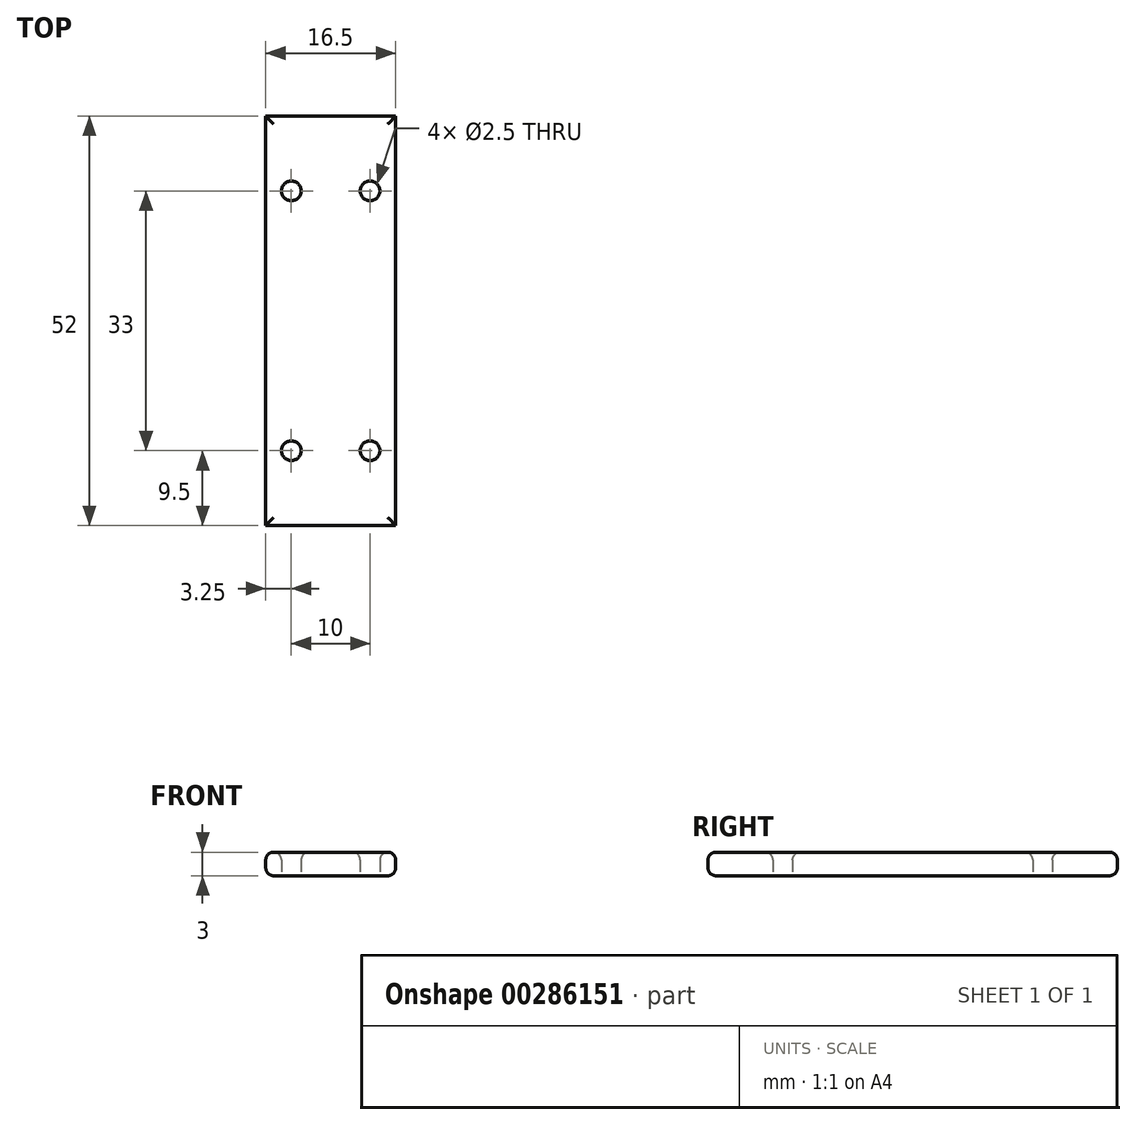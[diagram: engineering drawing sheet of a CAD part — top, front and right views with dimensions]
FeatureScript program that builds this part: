
annotation { "Feature Type Name" : "Feature", "Feature Type Description" : "" }
export const myFeature = defineFeature(function(context is Context, id is Id, definition is map)
    precondition{}
    {
        {
            var Q0;
            Q0=qCreatedBy(makeId("Top.planeOp"),FACE);
            var sketch = newSketch(context, id + "F0", { "sketchPlane" : qUnion([Q0])});
            skLineSegment(sketch, "E0.bottom", {"start": v(0, 0) * mm, "end": v(16.5, 0) * mm});
            skLineSegment(sketch, "E0.top", {"start": v(0, 52) * mm, "end": v(16.5, 52) * mm});
            skLineSegment(sketch, "E0.left", {"start": v(0, 0) * mm, "end": v(0, 52) * mm});
            skLineSegment(sketch, "E0.right", {"start": v(16.5, 0) * mm, "end": v(16.5, 52) * mm});
            skCircle(sketch, "E1", {"center": v(3.25, 9.5) * mm, "radius": 1.25 * mm});
            skLineSegment(sketch, "E2", {"start": v(8.25, 52) * mm, "end": v(8.25, 0) * mm, "construction": true});
            skLineSegment(sketch, "E3", {"start": v(0, 26) * mm, "end": v(16.5, 26) * mm, "construction": true});
            skCircle(sketch, "E4.MirrorC", {"center": v(13.25, 9.5) * mm, "radius": 1.25 * mm});
            skCircle(sketch, "E5.MirrorC", {"center": v(3.25, 42.5) * mm, "radius": 1.25 * mm});
            skCircle(sketch, "E6.MirrorC", {"center": v(13.25, 42.5) * mm, "radius": 1.25 * mm});
            skSolve(sketch);
        }
        {
            var Q0;
            Q0=makeQuery(id+"F0.imprint","IMPRINT",FACE,{"disambiguationData":[TD([[makeQuery(id+"F0.imprint","IMPRINT",EDGE,{"derivedFrom":sQuery(id+"F0.wireOp",EDGE,"E0.bottom")}),1.0]])]});
            extrude(context, id + "F1", {"entities" : qUnion([Q0]), "depth" : 3 * mm});
        }
        {
            var Q0;
            Q0=makeQuery(id+"F1.opExtrude","CAP_EDGE",EDGE,{"disambiguationData":[OSD([sQuery(id+"F0.wireOp",EDGE,"E0.right")])],"isStart":false});
            var Q1;
            Q1=makeQuery(id+"F1.opExtrude","CAP_EDGE",EDGE,{"disambiguationData":[OSD([sQuery(id+"F0.wireOp",EDGE,"E0.top")])],"isStart":false});
            var Q2;
            Q2=makeQuery(id+"F1.opExtrude","CAP_EDGE",EDGE,{"disambiguationData":[OSD([sQuery(id+"F0.wireOp",EDGE,"E0.left")])],"isStart":false});
            var Q3;
            Q3=makeQuery(id+"F1.opExtrude","CAP_FACE",FACE,{"disambiguationData":[OSD([sQuery(id+"F0.wireOp",EDGE,"E0.bottom"),sQuery(id+"F0.wireOp",EDGE,"E0.top"),sQuery(id+"F0.wireOp",EDGE,"E0.left"),sQuery(id+"F0.wireOp",EDGE,"E0.right"),sQuery(id+"F0.wireOp",EDGE,"E1"),sQuery(id+"F0.wireOp",EDGE,"E4.MirrorC"),sQuery(id+"F0.wireOp",EDGE,"E5.MirrorC"),sQuery(id+"F0.wireOp",EDGE,"E6.MirrorC")])],"isStart":false});
            var Q4;
            Q4=makeQuery(id+"F1.opExtrude","CAP_EDGE",EDGE,{"disambiguationData":[OSD([sQuery(id+"F0.wireOp",EDGE,"E0.right")])],"isStart":true});
            var Q5;
            Q5=makeQuery(id+"F1.opExtrude","CAP_EDGE",EDGE,{"disambiguationData":[OSD([sQuery(id+"F0.wireOp",EDGE,"E0.top")])],"isStart":true});
            var Q6;
            Q6=makeQuery(id+"F1.opExtrude","CAP_EDGE",EDGE,{"disambiguationData":[OSD([sQuery(id+"F0.wireOp",EDGE,"E0.left")])],"isStart":true});
            var Q7;
            Q7=makeQuery(id+"F1.opExtrude","CAP_EDGE",EDGE,{"disambiguationData":[OSD([sQuery(id+"F0.wireOp",EDGE,"E0.bottom")])],"isStart":true});
            fillet(context, id + "F2", {"entities" : qUnion([Q0, Q1, Q2, Q3, Q4, Q5, Q6, Q7]), "radius" : 1 * mm, "tangentPropagation" : true, "allowEdgeOverflow" : false});
        }
    });
